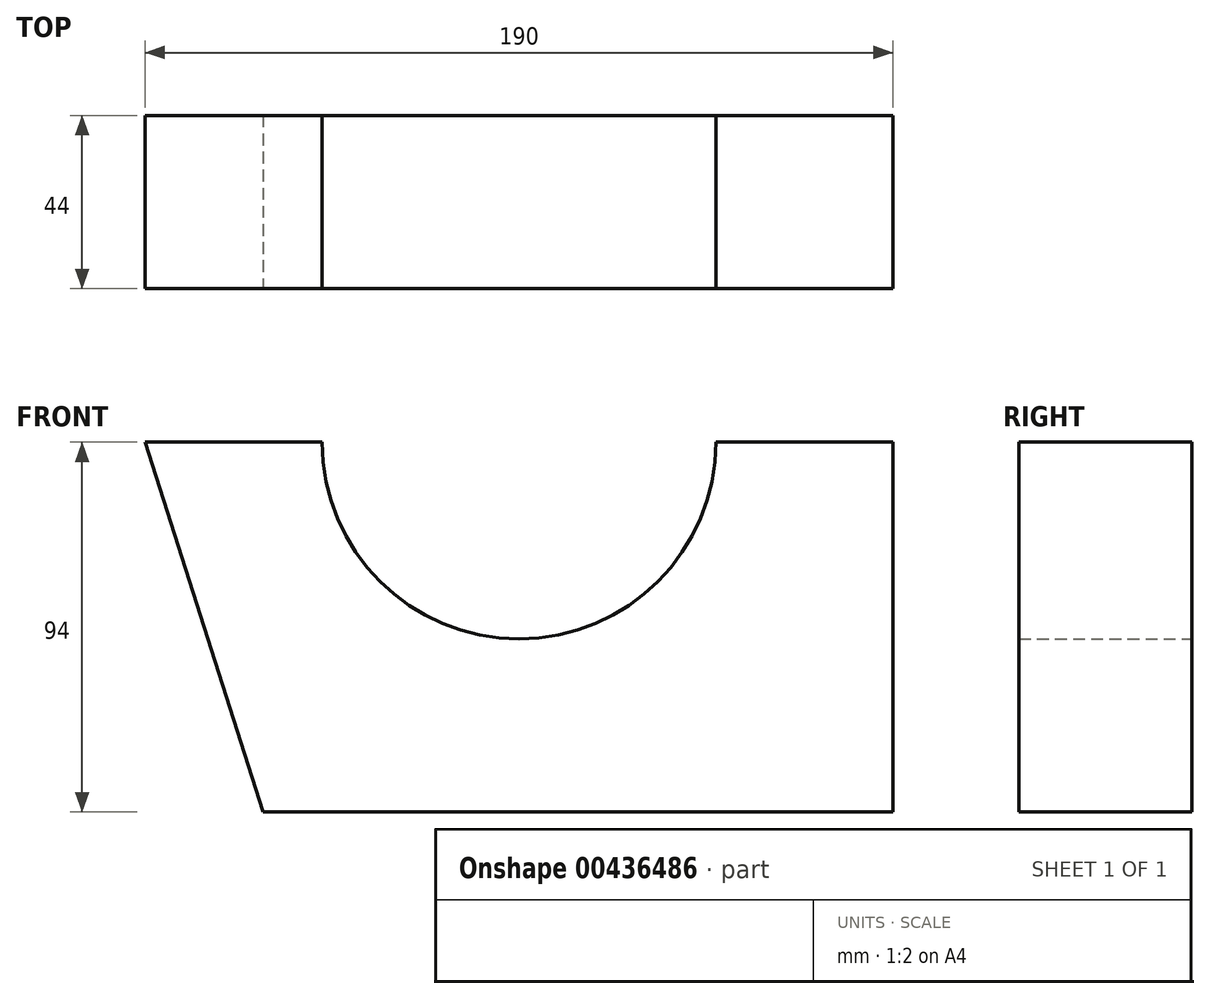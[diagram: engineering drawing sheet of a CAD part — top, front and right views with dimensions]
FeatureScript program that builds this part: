
annotation { "Feature Type Name" : "Feature", "Feature Type Description" : "" }
export const myFeature = defineFeature(function(context is Context, id is Id, definition is map)
    precondition{}
    {
        {
            var Q0;
            Q0=qCreatedBy(makeId("Front.planeOp"),FACE);
            var sketch = newSketch(context, id + "F0", { "sketchPlane" : qUnion([Q0])});
            skLineSegment(sketch, "E0.bottom", {"start": v(-95, 0) * mm, "end": v(95, 0) * mm});
            skLineSegment(sketch, "E0.top", {"start": v(-95, 94) * mm, "end": v(-50, 94) * mm});
            skLineSegment(sketch, "E0.left", {"start": v(-95, 0) * mm, "end": v(-95, 94) * mm});
            skLineSegment(sketch, "E0.right", {"start": v(95, 0) * mm, "end": v(95, 94) * mm});
            skArc(sketch, "E1", {"start": v(-50, 94) * mm, "mid": v(0, 44) * mm, "end": v(50, 94) * mm});
            skLineSegment(sketch, "E2.trimOffspring", {"start": v(50, 94) * mm, "end": v(95, 94) * mm});
            skSolve(sketch);
        }
        {
            var Q0;
            Q0 = qSketchRegion(id + "F0", true);
            extrude(context, id + "F1", {"entities" : qUnion([Q0]), "depth" : 44 * mm});
        }
        {
            var Q0;
            Q0=makeQuery(id+"F1.opExtrude","CAP_FACE",FACE,{"disambiguationData":[OSD([sQuery(id+"F0.wireOp",EDGE,"E0.bottom"),sQuery(id+"F0.wireOp",EDGE,"E0.top"),sQuery(id+"F0.wireOp",EDGE,"E0.left"),sQuery(id+"F0.wireOp",EDGE,"E0.right"),sQuery(id+"F0.wireOp",EDGE,"E1"),sQuery(id+"F0.wireOp",EDGE,"E2.trimOffspring")])],"isStart":false});
            var sketch = newSketch(context, id + "F2", { "sketchPlane" : qUnion([Q0])});
            skLineSegment(sketch, "E3", {"start": v(-95, 94) * mm, "end": v(-65, 0) * mm});
            skLineSegment(sketch, "E4", {"start": v(-65, 0) * mm, "end": v(-95, 0) * mm});
            skLineSegment(sketch, "E5", {"start": v(-95, 0) * mm, "end": v(-95, 94) * mm});
            skSolve(sketch);
        }
        {
            var Q0;
            Q0 = qSketchRegion(id + "F2", true);
            extrude(context, id + "F3", {"entities" : qUnion([Q0]), "operationType" : NewBodyOperationType.REMOVE, "endBound" : BoundingType.THROUGH_ALL, "oppositeDirection" : true, "depth" : 25.4 * mm});
        }
    });
